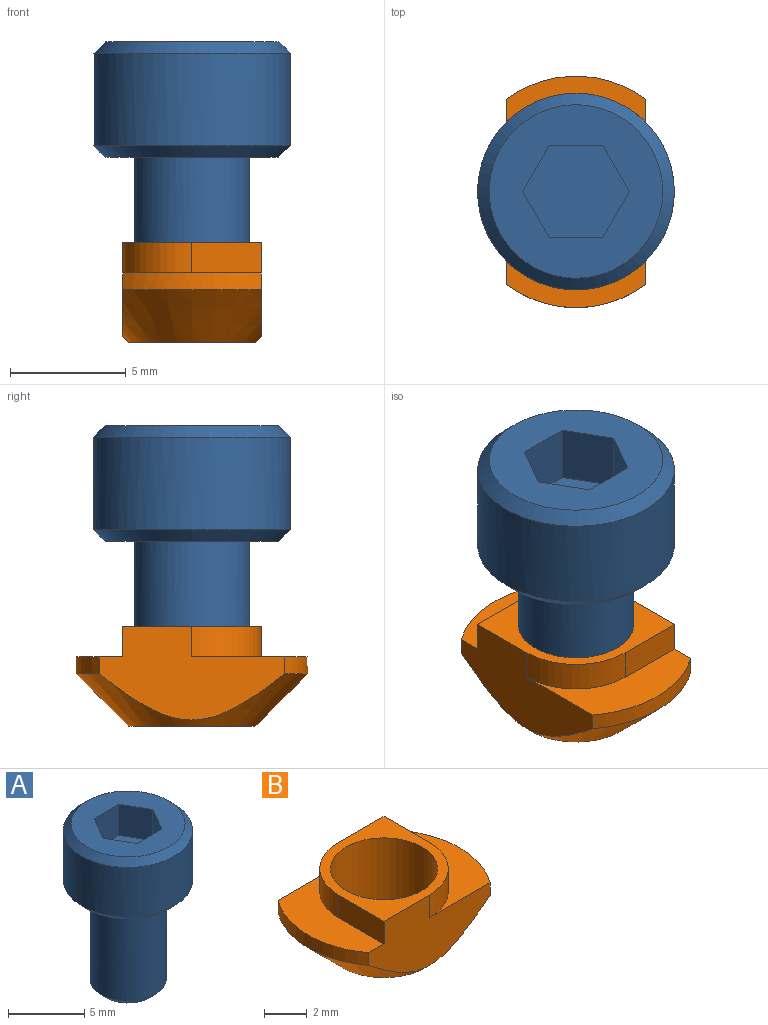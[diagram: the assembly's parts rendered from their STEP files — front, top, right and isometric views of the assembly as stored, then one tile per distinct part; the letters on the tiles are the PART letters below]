
ASSEMBLY  parts=2 mates=1
PART A: 15 faces, bbox 8.5x8.5x13 mm
  f0: plane 7.5x7.5mm, normal (0,0,1), area 30.3mm2, adj f5,f6,f7,f8,f9,f10,f14
  f1: plane 7.5x7.5mm, normal (0,0,-1), area 24.5mm2, adj f2,f13
  f2: cylinder r=2.5mm len=7.5mm, axis (0,0,1), area 117.8mm2, adj f1,f12
  f3: plane 4x4mm, normal (0,0,-1), area 12.6mm2, adj f12
  f4: cylinder r=4.25mm len=8.5mm, axis (0,0,1), area 106.8mm2, adj f13,f14
  f5: plane 2.5x2mm, normal (-0.87,0.5,0), area 5.8mm2, adj f0,f6,f10,f11
  f6: plane 2.5x2mm, normal (-0.87,-0.5,0), area 5.8mm2, adj f0,f5,f7,f11
  f7: plane 2.5x2.31mm, normal (0,-1,0), area 5.8mm2, adj f0,f6,f8,f11
  f8: plane 2.5x2mm, normal (0.87,-0.5,0), area 5.8mm2, adj f0,f7,f9,f11
  f9: plane 2.5x2mm, normal (0.87,0.5,0), area 5.8mm2, adj f0,f8,f10,f11
  f10: plane 2.5x2.31mm, normal (0,1,0), area 5.8mm2, adj f0,f5,f9,f11
  f11: plane 4.62x4mm, normal (0,0,1), area 13.9mm2, adj f5,f6,f7,f8,f9,f10
  f12: cone r=2.5mm half-angle=45deg, axis (0,0,1), area 10mm2, adj f2,f3
  f13: cone r=4.25mm half-angle=45deg, axis (0,0,1), area 17.8mm2, adj f1,f4
  f14: cone r=3.75mm half-angle=45deg, axis (0,0,-1), area 17.8mm2, adj f0,f4
PART B: 14 faces, bbox 10x10x4.3 mm
  f0: plane 6x5mm, normal (0,0,1), area 12mm2, adj f2,f6,f7,f9,f13
  f1: plane 6x5mm, normal (0,0,1), area 12mm2, adj f3,f6,f7,f8,f12
  f2: cylinder r=5mm len=6mm, axis (0,0,1), area 4.7mm2, adj f0,f4,f6,f7
  f3: cylinder r=5mm len=6mm, axis (0,0,1), area 4.7mm2, adj f1,f4,f6,f7
  f4: cone r=5mm half-angle=45deg, axis (0,0,1), area 46.4mm2, adj f2,f3,f5,f6,f7
  f5: plane 5.45x5.45mm, normal (0,0,-1), area 3.7mm2, adj f4,f11
  f6: plane 8.01x4.03mm, normal (0,1,0), area 19.8mm2, adj f0,f1,f2,f3,f4,f9,f10,f12
  f7: plane 8.01x4.03mm, normal (0,-1,0), area 19.8mm2, adj f0,f1,f2,f3,f4,f8,f10,f13
  f8: plane 3x1.3mm, normal (-1,0,0), area 3.9mm2, adj f1,f7,f10,f12
  f9: plane 3x1.3mm, normal (1,0,0), area 3.9mm2, adj f0,f6,f10,f13
  f10: plane 6x6mm, normal (0,0,1), area 12.5mm2, adj f6,f7,f8,f9,f11,f12,f13
  f11: cylinder r=2.5mm len=5mm, axis (0,0,-1), area 67.5mm2, adj f5,f10
  f12: cylinder r=3mm len=3mm, axis (0,0,-1), area 6.1mm2, adj f1,f6,f8,f10
  f13: cylinder r=3mm len=3mm, axis (0,0,-1), area 6.1mm2, adj f0,f7,f9,f10
PLACE A t=(-28.8,-44.24,-46.78)mm
PLACE B rot(axis=(0,0,-1),90deg) t=(-28.8,-44.24,-54.98)mm
MATE fastened B.f2 <-> A.f2  axis (0,0,-1) through (-28.8,-44.24,-49.78)mm
